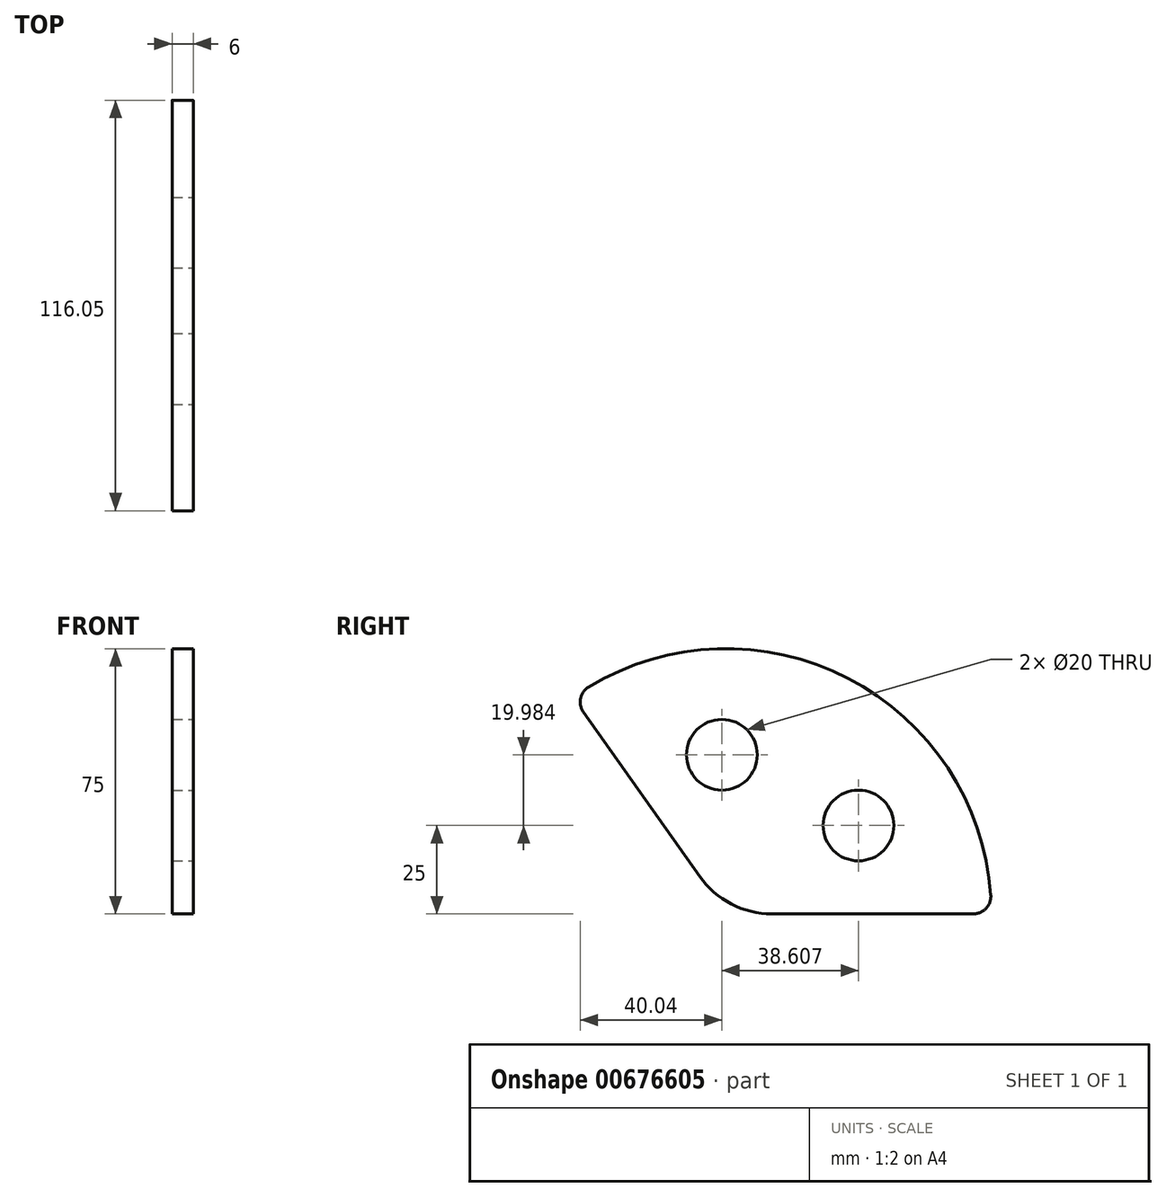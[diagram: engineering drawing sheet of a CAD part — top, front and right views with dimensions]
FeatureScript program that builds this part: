
annotation { "Feature Type Name" : "Feature", "Feature Type Description" : "" }
export const myFeature = defineFeature(function(context is Context, id is Id, definition is map)
    precondition{}
    {
        {
            var Q0;
            Q0=qCreatedBy(makeId("Right.planeOp"),FACE);
            var sketch = newSketch(context, id + "F0", { "sketchPlane" : qUnion([Q0])});
            skLineSegment(sketch, "E0", {"start": v(0, 0) * mm, "end": v(75, 0) * mm});
            skLineSegment(sketch, "E1", {"start": v(0, 0) * mm, "end": v(-43.3, 61.24) * mm});
            skArc(sketch, "E2", {"start": v(75, 0) * mm, "mid": v(34.48, 66.6) * mm, "end": v(-43.3, 61.24) * mm});
            skSolve(sketch);
        }
        {
            var Q0;
            Q0=makeQuery(id+"F0.imprint","IMPRINT",FACE,{"disambiguationData":[TD([[makeQuery(id+"F0.imprint","IMPRINT",EDGE,{"derivedFrom":sQuery(id+"F0.wireOp",EDGE,"E0")}),1.0]])]});
            extrude(context, id + "F1", {"entities" : qUnion([Q0]), "depth" : 6 * mm, "offsetDistance" : 25 * mm});
        }
        {
            var Q0;
            Q0=makeQuery(id+"F1.opExtrude","SWEPT_EDGE",EDGE,{"disambiguationData":[OSD([sQuery(id+"F0.wireOp",EDGE,"E0"),sQuery(id+"F0.wireOp",EDGE,"E1")])]});
            fillet(context, id + "F2", {"entities" : qUnion([Q0]), "radius" : 25 * mm, "tangentPropagation" : true, "allowEdgeOverflow" : false});
        }
        {
            var Q0;
            Q0=makeQuery(id+"F1.opExtrude","SWEPT_EDGE",EDGE,{"disambiguationData":[OSD([sQuery(id+"F0.wireOp",EDGE,"E1"),sQuery(id+"F0.wireOp",EDGE,"E2")])]});
            var Q1;
            Q1=makeQuery(id+"F1.opExtrude","SWEPT_EDGE",EDGE,{"disambiguationData":[OSD([sQuery(id+"F0.wireOp",EDGE,"E0"),sQuery(id+"F0.wireOp",EDGE,"E2")])]});
            fillet(context, id + "F3", {"entities" : qUnion([Q0, Q1]), "radius" : 5 * mm, "tangentPropagation" : true, "allowEdgeOverflow" : false});
        }
        {
            var Q0;
            Q0=makeQuery(id+"F1.opExtrude","CAP_FACE",FACE,{"disambiguationData":[OSD([sQuery(id+"F0.wireOp",EDGE,"E0"),sQuery(id+"F0.wireOp",EDGE,"E1"),sQuery(id+"F0.wireOp",EDGE,"E2")])],"isStart":false});
            var sketch = newSketch(context, id + "F4", { "sketchPlane" : qUnion([Q0])});
            skCircle(sketch, "E3", {"center": v(-1.2, 44.98) * mm, "radius": 10 * mm});
            skCircle(sketch, "E4", {"center": v(37.42, 25) * mm, "radius": 10 * mm});
            skSolve(sketch);
        }
        {
            var Q0;
            Q0 = qSketchRegion(id + "F4", true);
            extrude(context, id + "F5", {"entities" : qUnion([Q0]), "operationType" : NewBodyOperationType.REMOVE, "endBound" : BoundingType.THROUGH_ALL, "oppositeDirection" : true, "depth" : 25 * mm, "offsetDistance" : 25 * mm});
        }
    });
